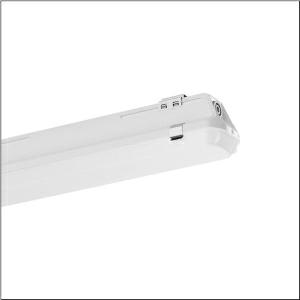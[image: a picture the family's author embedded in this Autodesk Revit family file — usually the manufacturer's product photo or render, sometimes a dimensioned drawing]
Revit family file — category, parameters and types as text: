
# Revit family: monsun_r__21_51fb107p480b_58b6
name_source: partatom
category: Lighting Fixtures
units: mm (PartAtom-declared; Revit-internal decimal feet)

## family parameters
Cut with Voids When Loaded = No
Host = Face
Light Source = No
Part Type = Normal
Room Calculation Point = No
Round Connector Dimension = Use Diameter
Shared = No

## types (1)
- Monsun® 21 (1 x LED, 8070 lm, 52.8 W, 4000K)
    Apparent Load = 53 VA
    CIE Flux Codes = 47 77 93 94 100
    Color Rendering = 80
    Color Temperature = 4000K
    Default Elevation = 1800 mm
    Description = Monsun® 21, damp-proof luminaire, chain hanger, primary optical cover: enclosure, of PMMA, light emission: direct distribution, primary light characteristic: symmetric, installation type: suspended mounting, surface-mounted, horizontal mounting, vertical mounting, LED, rated luminous flux: 8.070lm, luminous efficacy: 153lm/W, light colour: 840, colour temperature: 4000K, control gear: ECG, with terminal, 3-pole, max. 2.5mm², mains connection: 220..240V, AC, 50/60Hz, rated input power: 53W, housing, of glass-fibre reinforced polyester, uncoated, bright grey, incl. chain hanger, length: 1.590mm, width: 90mm, height: 88mm, clip for enclosure, of stainless steel (V2A), ceiling mounting element, of stainless steel (V2A), chain hanger, of stainless steel (V2A), protection rating (complete): IP66, insulation class (complete): insulation class I (protective earthing), certification: CE, ENEC, VDE, UKCA, protection symbol: D, impact resistance: IK04, permissible operating ambient temperature: -25..+35°C, standard: EN 50419, EN 60598-2-1, corresponds to IFS (International Featured Standards) requirements for safety and quality in the food industry, for indoor or canopied outdoor use, no direct snow, no direct sun, no direct rain, contact your sales advisor before using the luminaires in applications with unclear chemical exposure, large temperature fluctuations or condensation-forming humidity, LABS conformity tested according to VDMA 24364:2018-05, packaging unit: 1 piece
    Height = 89 mm
    Lamp = 1 x LED
    Lamp Light Flux = 8070 lm
    Lamp Power = 52.8 W
    Lamp count = 1
    Length = 1590 mm
    Luminous efficacy = 153 lm/W
    Manufacturer = Siteco
    ModVariant = No
    Model = 51FB107P480B
    Mounting Place = Ceiling
    Mounting Type = Surface mounted
    Number of Poles = 1
    OnlyDefault = Yes
    Power Factor = 1
    Product Name = Monsun® 21
    Product group = damp-proof luminaire
    ProductGroupID = 301
    Protection Class = Protection class I
    Protection Degree = IP 66
    RLX_Detail_Level = 1
    RLX_Emergency_Light_Flux = 0 lm
    RLX_Emergency_Type = 0
    RLX_Emergency_Type_DB = No
    RlxData = <blob elided: 88509 chars, md5=7d43a32b>
    Socket = socket
    Standby Power = 0 W
    System Light Flux = 8070 lm
    System Power = 53 W
    Type Comments = Product without accessories
    Type Image = l_1006717.jpg
    URL = http://relux.com
    VarID = ---
    Voltage = 0 V
    Weight = 0.00 kg
    Width = 90 mm

## geometry (parser evidence)
native form markers: Blend x4, Sweep x13
no freeform markers — native parametric forms only
